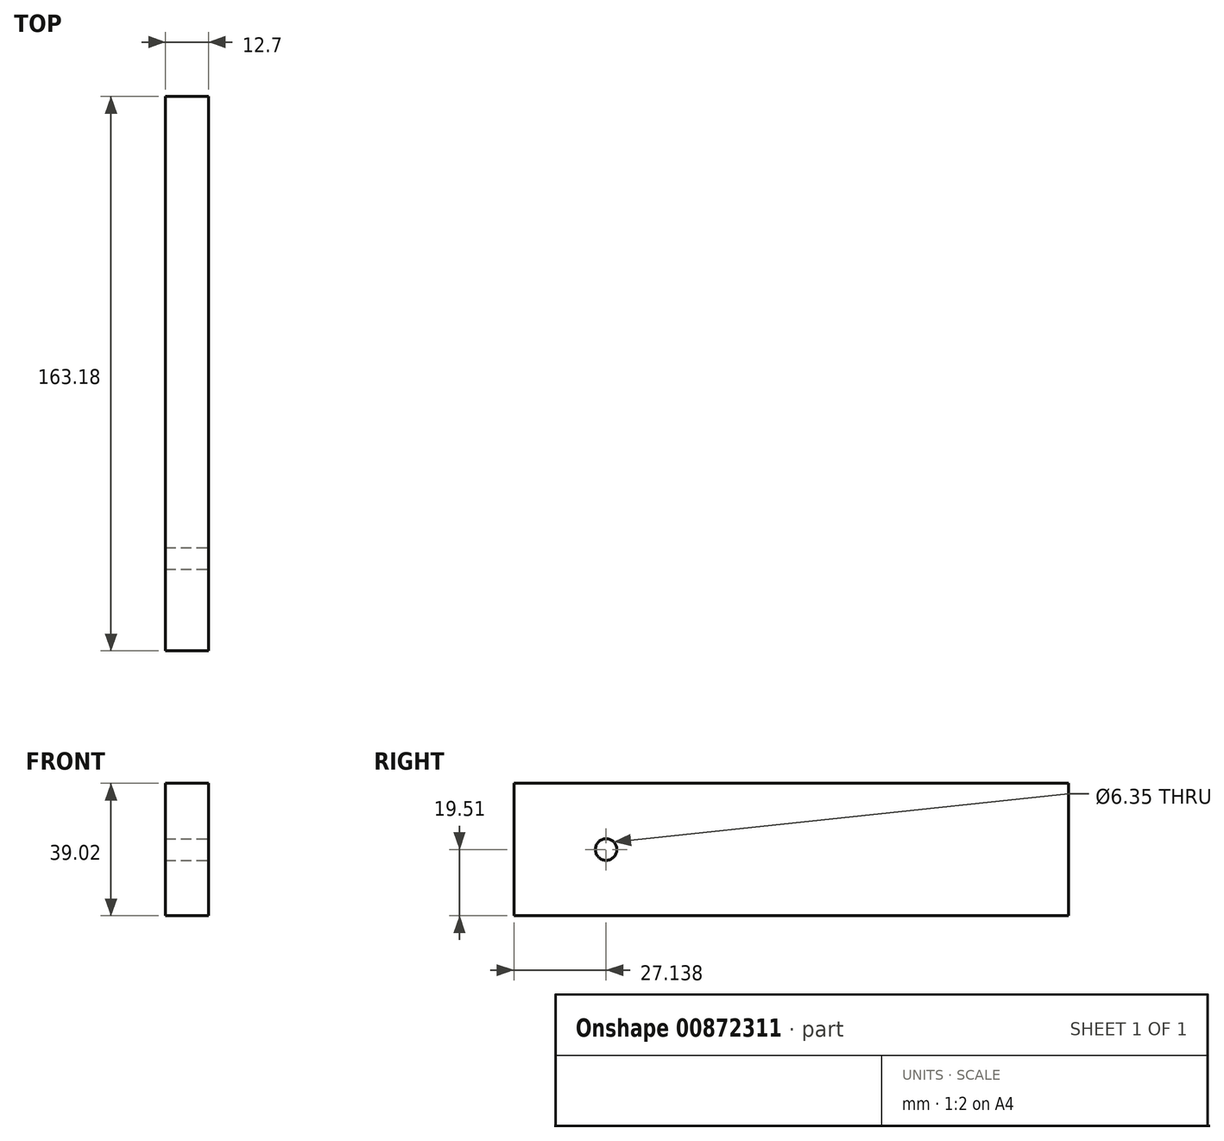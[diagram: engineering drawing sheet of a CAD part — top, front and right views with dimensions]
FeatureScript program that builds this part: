
annotation { "Feature Type Name" : "Feature", "Feature Type Description" : "" }
export const myFeature = defineFeature(function(context is Context, id is Id, definition is map)
    precondition{}
    {
        {
            var Q0;
            Q0=qCreatedBy(makeId("Right.planeOp"),FACE);
            var sketch = newSketch(context, id + "F0", { "sketchPlane" : qUnion([Q0])});
            skLineSegment(sketch, "E0.bottom", {"start": v(0, 70.68) * mm, "end": v(-163.17, 70.68) * mm});
            skLineSegment(sketch, "E0.top", {"start": v(0, 31.65) * mm, "end": v(-163.17, 31.65) * mm});
            skLineSegment(sketch, "E0.left", {"start": v(0, 70.68) * mm, "end": v(0, 31.65) * mm});
            skLineSegment(sketch, "E0.right", {"start": v(-163.17, 70.68) * mm, "end": v(-163.17, 31.65) * mm});
            skPoint(sketch, "E0.middle", {"position": v(-81.59, 51.16) * mm});
            skLineSegment(sketch, "E1.bottom", {"start": v(81.59, 19.51) * mm, "end": v(-81.59, 19.51) * mm});
            skLineSegment(sketch, "E1.top", {"start": v(81.59, -19.51) * mm, "end": v(-81.59, -19.51) * mm});
            skLineSegment(sketch, "E1.left", {"start": v(81.59, 19.51) * mm, "end": v(81.59, -19.51) * mm});
            skLineSegment(sketch, "E1.right", {"start": v(-81.59, 19.51) * mm, "end": v(-81.59, -19.51) * mm});
            skPoint(sketch, "E1.middle", {"position": v(0, 0) * mm});
            skSolve(sketch);
        }
        {
            var Q0;
            Q0=makeQuery(id+"F0.imprint","IMPRINT",FACE,{"disambiguationData":[TD([[makeQuery(id+"F0.imprint","IMPRINT",EDGE,{"derivedFrom":sQuery(id+"F0.wireOp",EDGE,"E1.bottom")}),1.0]])]});
            var Q1;
            Q1=sQuery(id+"F0.wireOp",EDGE,"E1.left");
            var Q2;
            Q2=sQuery(id+"F0.wireOp",EDGE,"E1.bottom");
            var Q3;
            Q3=sQuery(id+"F0.wireOp",EDGE,"E1.right");
            var Q4;
            Q4=sQuery(id+"F0.wireOp",EDGE,"E1.top");
            extrude(context, id + "F1", {"entities" : qUnion([Q0]), "surfaceEntities" : qUnion([Q1, Q2, Q3, Q4]), "depth" : 12.7 * mm, "offsetDistance" : 25.4 * mm});
        }
        {
            var Q0;
            Q0=makeQuery(id+"F1.opExtrude","CAP_FACE",FACE,{"disambiguationData":[OSD([sQuery(id+"F0.wireOp",EDGE,"E1.bottom"),sQuery(id+"F0.wireOp",EDGE,"E1.top"),sQuery(id+"F0.wireOp",EDGE,"E1.left"),sQuery(id+"F0.wireOp",EDGE,"E1.right")])],"isStart":false});
            var sketch = newSketch(context, id + "F2", { "sketchPlane" : qUnion([Q0])});
            skCircle(sketch, "E2", {"center": v(-54.45, 0) * mm, "radius": 9.16 * mm});
            skPoint(sketch, "E2.centerSnap0", {"position": v(-81.59, 0) * mm});
            skSolve(sketch);
        }
        {
            var Q0;
            Q0=sQuery(id+"F2.wireOp",VERTEX,"E2.center");
            var Q1;
            Q1=makeQuery(id+"F1.opExtrude","SWEPT_BODY",BODY,{"disambiguationData":[OSD([sQuery(id+"F0.wireOp",EDGE,"E1.bottom"),sQuery(id+"F0.wireOp",EDGE,"E1.top"),sQuery(id+"F0.wireOp",EDGE,"E1.left"),sQuery(id+"F0.wireOp",EDGE,"E1.right")])]});
            hole(context, id + "F3", {"style" : HoleStyle.SIMPLE, "endStyle" : HoleEndStyle.THROUGH, "holeDiameter" : 6.35 * mm, "majorDiameter" : 6.35 * mm, "isTappedThrough" : true, "tappedDepth" : 12.7 * mm, "tapClearance" : 3, "locations" : qUnion([Q0]), "scope" : qUnion([Q1])});
        }
    });
